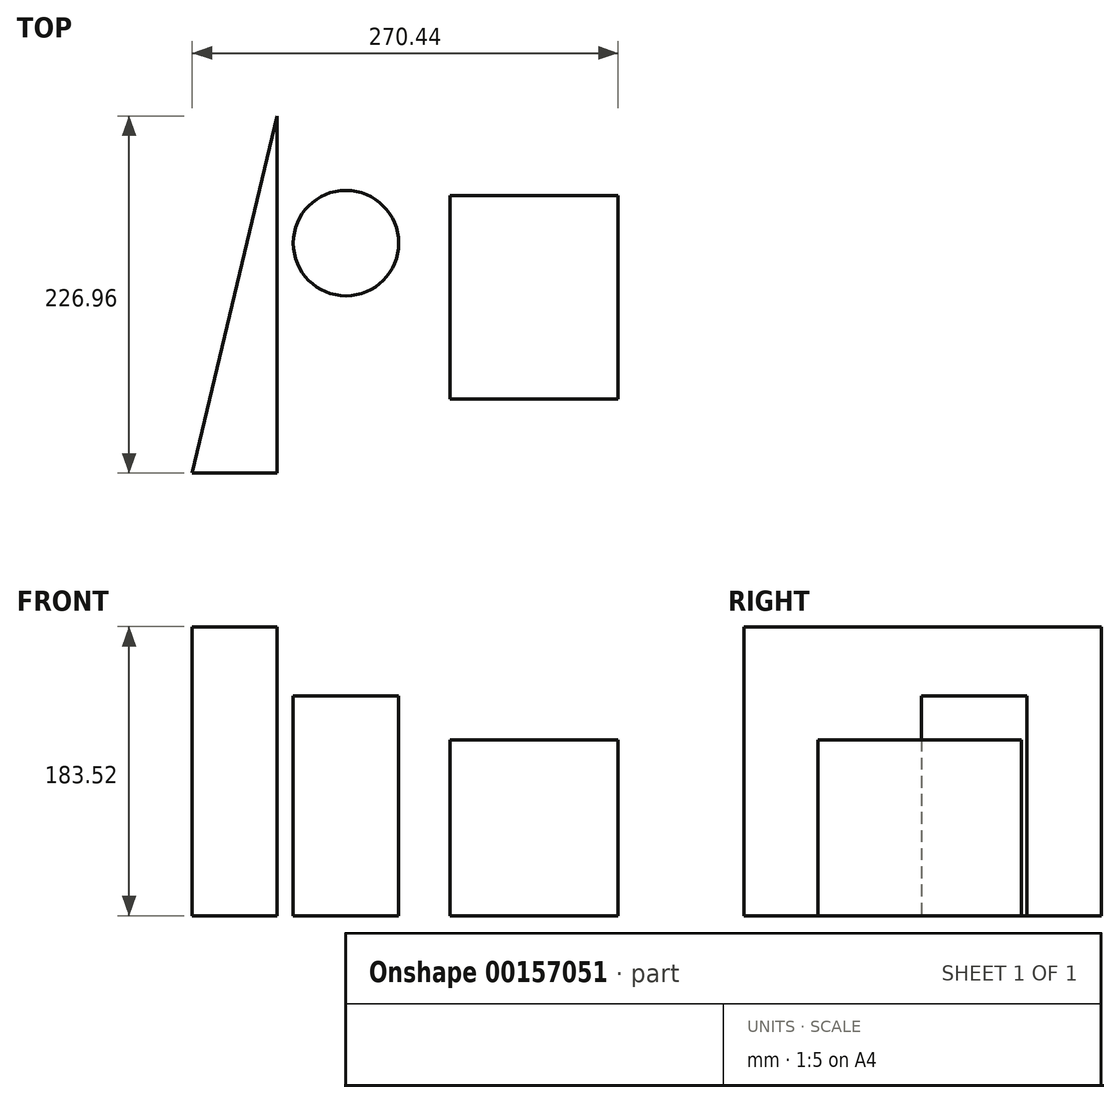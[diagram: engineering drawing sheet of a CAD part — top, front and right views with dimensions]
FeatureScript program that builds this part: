
annotation { "Feature Type Name" : "Feature", "Feature Type Description" : "" }
export const myFeature = defineFeature(function(context is Context, id is Id, definition is map)
    precondition{}
    {
        {
            var Q0;
            Q0=qCreatedBy(makeId("Top.planeOp"),FACE);
            var sketch = newSketch(context, id + "F0", { "sketchPlane" : qUnion([Q0])});
            skLineSegment(sketch, "E0.bottom", {"start": v(-53.38, 56.42) * mm, "end": v(53.38, 56.42) * mm});
            skLineSegment(sketch, "E0.top", {"start": v(-53.38, -72.91) * mm, "end": v(53.38, -72.91) * mm});
            skLineSegment(sketch, "E0.left", {"start": v(-53.38, 56.42) * mm, "end": v(-53.38, -72.91) * mm});
            skLineSegment(sketch, "E0.right", {"start": v(53.38, 56.42) * mm, "end": v(53.38, -72.91) * mm});
            skSolve(sketch);
        }
        {
            var Q0;
            Q0=makeQuery(id+"F0.imprint","IMPRINT",FACE,{"disambiguationData":[TD([[makeQuery(id+"F0.imprint","IMPRINT",EDGE,{"derivedFrom":sQuery(id+"F0.wireOp",EDGE,"E0.bottom")}),-1.0]])]});
            extrude(context, id + "F1", {"entities" : qUnion([Q0]), "depth" : 111.76 * mm});
        }
        {
            var Q0;
            Q0=qCreatedBy(makeId("Top.planeOp"),FACE);
            var sketch = newSketch(context, id + "F2", { "sketchPlane" : qUnion([Q0])});
            skCircle(sketch, "E1", {"center": v(-119.37, 26.26) * mm, "radius": 33.5 * mm});
            skSolve(sketch);
        }
        {
            var Q0;
            Q0=makeQuery(id+"F2.imprint","IMPRINT",FACE,{"disambiguationData":[TD([[makeQuery(id+"F2.imprint","IMPRINT",EDGE,{"derivedFrom":sQuery(id+"F2.wireOp",EDGE,"E1")}),1.0]])]});
            extrude(context, id + "F3", {"entities" : qUnion([Q0]), "depth" : 139.7 * mm});
        }
        {
            var Q0;
            Q0=qCreatedBy(makeId("Top.planeOp"),FACE);
            var sketch = newSketch(context, id + "F4", { "sketchPlane" : qUnion([Q0])});
            skLineSegment(sketch, "E2.bottom", {"start": v(-217.06, 107.07) * mm, "end": v(-163.1, 107.07) * mm});
            skLineSegment(sketch, "E2.top", {"start": v(-217.06, -119.9) * mm, "end": v(-163.1, -119.9) * mm});
            skLineSegment(sketch, "E2.left", {"start": v(-217.06, 107.07) * mm, "end": v(-217.06, -119.9) * mm});
            skLineSegment(sketch, "E2.right", {"start": v(-163.1, 107.07) * mm, "end": v(-163.1, -119.9) * mm});
            skLineSegment(sketch, "E3", {"start": v(-163.1, 107.07) * mm, "end": v(-217.06, -119.9) * mm});
            skSolve(sketch);
        }
        {
            var Q0;
            Q0=makeQuery(id+"F4.imprint","IMPRINT",FACE,{"disambiguationData":[TD([[makeQuery(id+"F4.imprint","IMPRINT",EDGE,{"derivedFrom":sQuery(id+"F4.wireOp",EDGE,"E2.top")}),1.0]])]});
            extrude(context, id + "F5", {"entities" : qUnion([Q0]), "depth" : 183.5 * mm});
        }
    });
